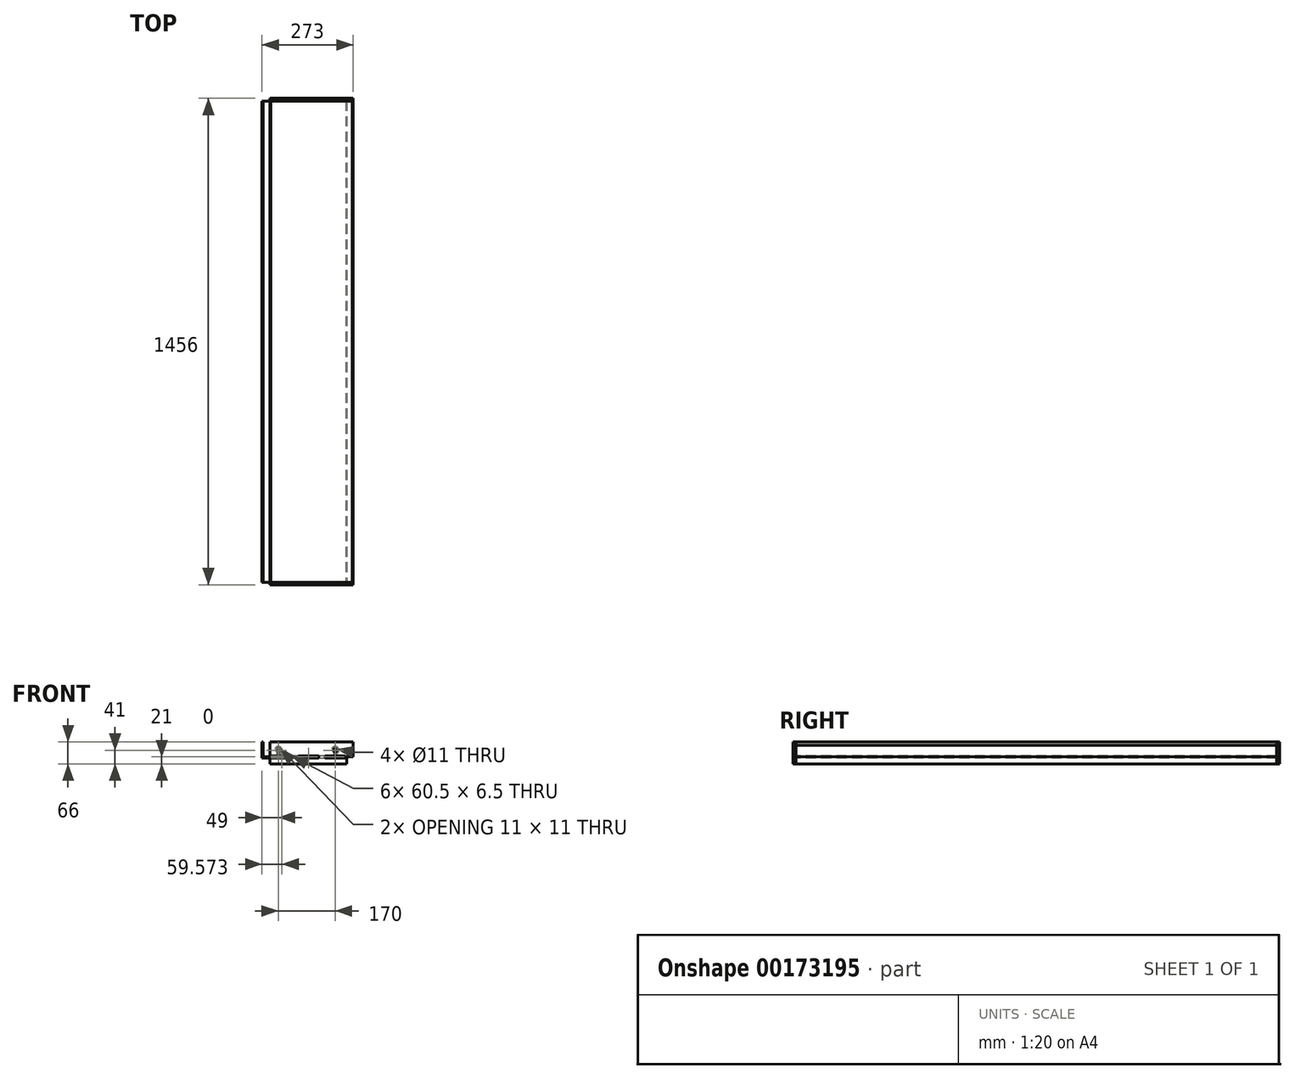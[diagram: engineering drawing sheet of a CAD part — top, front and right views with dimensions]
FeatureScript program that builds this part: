
annotation { "Feature Type Name" : "Feature", "Feature Type Description" : "" }
export const myFeature = defineFeature(function(context is Context, id is Id, definition is map)
    precondition{}
    {
        {
            var Q0;
            Q0=qCreatedBy(makeId("Front.planeOp"),FACE);
            var sketch = newSketch(context, id + "F0", { "sketchPlane" : qUnion([Q0])});
            skLineSegment(sketch, "E0", {"start": v(0, 48) * mm, "end": v(0, 0) * mm});
            skLineSegment(sketch, "E1", {"start": v(0, 0) * mm, "end": v(251, 0) * mm});
            skLineSegment(sketch, "E2", {"start": v(251, 0) * mm, "end": v(251, -18) * mm});
            skLineSegment(sketch, "E3", {"start": v(251, -18) * mm, "end": v(254, -18) * mm});
            skLineSegment(sketch, "E4", {"start": v(254, -18) * mm, "end": v(254, 3) * mm});
            skLineSegment(sketch, "E5", {"start": v(273, 3) * mm, "end": v(273, 0) * mm});
            skLineSegment(sketch, "E6", {"start": v(254, 3) * mm, "end": v(3, 3) * mm});
            skLineSegment(sketch, "E7", {"start": v(27, 48) * mm, "end": v(24, 48) * mm});
            skLineSegment(sketch, "E8", {"start": v(3, 3) * mm, "end": v(3, 48) * mm});
            skLineSegment(sketch, "E9", {"start": v(3, 48) * mm, "end": v(0, 48) * mm});
            skPoint(sketch, "E10.start.orphan", {"position": v(254, 0) * mm});
            skLineSegment(sketch, "E11", {"start": v(24, 48) * mm, "end": v(24, 3) * mm});
            skLineSegment(sketch, "E12", {"start": v(24, 3) * mm, "end": v(273, 3) * mm});
            skLineSegment(sketch, "E13", {"start": v(273, 3) * mm, "end": v(273, 6) * mm});
            skLineSegment(sketch, "E14", {"start": v(270, 6) * mm, "end": v(27, 6) * mm});
            skLineSegment(sketch, "E15", {"start": v(27, 6) * mm, "end": v(27, 48) * mm});
            skLineSegment(sketch, "E16", {"start": v(273, 6) * mm, "end": v(273, 38) * mm});
            skLineSegment(sketch, "E17", {"start": v(273, 38) * mm, "end": v(270, 38) * mm});
            skLineSegment(sketch, "E18", {"start": v(270, 38) * mm, "end": v(270, 6) * mm});
            skSolve(sketch);
        }
        {
            var Q0;
            Q0=makeQuery(id+"F0.imprint","IMPRINT",FACE,{"disambiguationData":[TD([[makeQuery(id+"F0.imprint","IMPRINT",EDGE,{"derivedFrom":sQuery(id+"F0.wireOp",EDGE,"E0")}),1.0]])]});
            extrude(context, id + "F1", {"entities" : qUnion([Q0]), "oppositeDirection" : true, "depth" : 1440 * mm});
        }
        {
            var Q0;
            Q0=makeQuery(id+"F0.imprint","IMPRINT",FACE,{"disambiguationData":[TD([[makeQuery(id+"F0.imprint","IMPRINT",EDGE,{"derivedFrom":sQuery(id+"F0.wireOp",EDGE,"E7")}),1.0]])]});
            extrude(context, id + "F2", {"entities" : qUnion([Q0]), "oppositeDirection" : true, "depth" : 1440 * mm});
        }
        {
            var Q0;
            Q0=makeQuery(id+"F2.opExtrude","SWEPT_FACE",FACE,{"disambiguationData":[OSD([sQuery(id+"F0.wireOp",EDGE,"E12")])]});
            var sketch = newSketch(context, id + "F3", { "sketchPlane" : qUnion([Q0])});
            skLineSegment(sketch, "E19.bottom", {"start": v(29.57, 7) * mm, "end": v(89.57, 7) * mm});
            skLineSegment(sketch, "E19.top", {"start": v(29.57, 0) * mm, "end": v(89.57, 0) * mm});
            skLineSegment(sketch, "E19.left", {"start": v(29.57, 7) * mm, "end": v(29.57, 0) * mm});
            skLineSegment(sketch, "E19.right", {"start": v(89.57, 7) * mm, "end": v(89.57, 0) * mm});
            skLineSegment(sketch, "E20.1.0.0", {"start": v(169.57, 7) * mm, "end": v(169.57, 0) * mm});
            skLineSegment(sketch, "E20.1.0.1", {"start": v(109.57, 7) * mm, "end": v(109.57, 0) * mm});
            skLineSegment(sketch, "E20.1.0.2", {"start": v(109.57, 0) * mm, "end": v(169.57, 0) * mm});
            skLineSegment(sketch, "E20.1.0.3", {"start": v(109.57, 7) * mm, "end": v(169.57, 7) * mm});
            skLineSegment(sketch, "E20.2.0.0", {"start": v(249, 7) * mm, "end": v(249, 0) * mm});
            skLineSegment(sketch, "E20.2.0.1", {"start": v(189, 7) * mm, "end": v(189, 0) * mm});
            skLineSegment(sketch, "E20.2.0.2", {"start": v(189, 0) * mm, "end": v(249, 0) * mm});
            skLineSegment(sketch, "E20.2.0.3", {"start": v(189, 7) * mm, "end": v(249, 7) * mm});
            skLineSegment(sketch, "E21", {"start": v(24, -720) * mm, "end": v(-373.93, -720) * mm, "construction": true});
            skLineSegment(sketch, "E22.MirrorCS", {"start": v(189, -1447) * mm, "end": v(189, -1440) * mm});
            skLineSegment(sketch, "E23.MirrorCS", {"start": v(29.57, -1447) * mm, "end": v(29.57, -1440) * mm});
            skLineSegment(sketch, "E24.MirrorCS", {"start": v(169.57, -1447) * mm, "end": v(169.57, -1440) * mm});
            skLineSegment(sketch, "E25.MirrorCS", {"start": v(109.57, -1447) * mm, "end": v(109.57, -1440) * mm});
            skLineSegment(sketch, "E26.MirrorCS", {"start": v(249, -1447) * mm, "end": v(249, -1440) * mm});
            skLineSegment(sketch, "E27.MirrorCS", {"start": v(89.57, -1447) * mm, "end": v(89.57, -1440) * mm});
            skLineSegment(sketch, "E28.MirrorCS", {"start": v(189, -1440) * mm, "end": v(249, -1440) * mm});
            skLineSegment(sketch, "E29.MirrorCS", {"start": v(109.57, -1440) * mm, "end": v(169.57, -1440) * mm});
            skLineSegment(sketch, "E30.MirrorCS", {"start": v(29.57, -1447) * mm, "end": v(89.57, -1447) * mm});
            skLineSegment(sketch, "E31.MirrorCS", {"start": v(189, -1447) * mm, "end": v(249, -1447) * mm});
            skLineSegment(sketch, "E32.MirrorCS", {"start": v(109.57, -1447) * mm, "end": v(169.57, -1447) * mm});
            skLineSegment(sketch, "E33.MirrorCS", {"start": v(29.57, -1440) * mm, "end": v(89.57, -1440) * mm});
            skSolve(sketch);
        }
        {
            var Q0;
            Q0 = qSketchRegion(id + "F3", true);
            extrude(context, id + "F4", {"entities" : qUnion([Q0]), "operationType" : NewBodyOperationType.ADD, "oppositeDirection" : true, "depth" : 3 * mm});
        }
        {
            var Q0;
            Q0=sQuery(id+"F3.wireOp",EDGE,"E21");
            cPlane(context, id + "F5", {"entities" : qUnion([Q0]), "cplaneType" : CPlaneType.LINE_ANGLE, "offset" : 25 * mm, "angle" : 0 * degree, "width" : 150 * mm, "height" : 150 * mm});
        }
        {
            var Q0;
            Q0=makeQuery(id+"F1.opExtrude","SWEPT_FACE",FACE,{"disambiguationData":[OSD([sQuery(id+"F0.wireOp",EDGE,"E1")])]});
            var sketch = newSketch(context, id + "F6", { "sketchPlane" : qUnion([Q0])});
            skLineSegment(sketch, "E34.bottom", {"start": v(249, 0) * mm, "end": v(189, 0) * mm});
            skLineSegment(sketch, "E34.top", {"start": v(249, 7) * mm, "end": v(189, 7) * mm});
            skLineSegment(sketch, "E34.left", {"start": v(249, 0) * mm, "end": v(249, 7) * mm});
            skLineSegment(sketch, "E34.right", {"start": v(189, 0) * mm, "end": v(189, 7) * mm});
            skLineSegment(sketch, "E35.bottom", {"start": v(169.57, 0) * mm, "end": v(109.57, 0) * mm});
            skLineSegment(sketch, "E35.top", {"start": v(169.57, 7) * mm, "end": v(109.57, 7) * mm});
            skLineSegment(sketch, "E35.left", {"start": v(169.57, 0) * mm, "end": v(169.57, 7) * mm});
            skLineSegment(sketch, "E35.right", {"start": v(109.57, 0) * mm, "end": v(109.57, 7) * mm});
            skLineSegment(sketch, "E36.bottom", {"start": v(89.57, 0) * mm, "end": v(29.57, 0) * mm});
            skLineSegment(sketch, "E36.top", {"start": v(89.57, 7) * mm, "end": v(29.57, 7) * mm});
            skLineSegment(sketch, "E36.left", {"start": v(89.57, 0) * mm, "end": v(89.57, 7) * mm});
            skLineSegment(sketch, "E36.right", {"start": v(29.57, 0) * mm, "end": v(29.57, 7) * mm});
            skLineSegment(sketch, "E37.MirrorCS", {"start": v(249, -1440) * mm, "end": v(249, -1447) * mm});
            skLineSegment(sketch, "E38.MirrorCS", {"start": v(29.57, -1440) * mm, "end": v(29.57, -1447) * mm});
            skLineSegment(sketch, "E39.MirrorCS", {"start": v(89.57, -1440) * mm, "end": v(89.57, -1447) * mm});
            skLineSegment(sketch, "E40.MirrorCS", {"start": v(169.57, -1440) * mm, "end": v(169.57, -1447) * mm});
            skLineSegment(sketch, "E41.MirrorCS", {"start": v(109.57, -1440) * mm, "end": v(109.57, -1447) * mm});
            skLineSegment(sketch, "E42.MirrorCS", {"start": v(189, -1440) * mm, "end": v(189, -1447) * mm});
            skLineSegment(sketch, "E43.MirrorCS", {"start": v(249, -1440) * mm, "end": v(189, -1440) * mm});
            skLineSegment(sketch, "E44.MirrorCS", {"start": v(249, -1447) * mm, "end": v(189, -1447) * mm});
            skLineSegment(sketch, "E45.MirrorCS", {"start": v(89.57, -1447) * mm, "end": v(29.57, -1447) * mm});
            skLineSegment(sketch, "E46.MirrorCS", {"start": v(169.57, -1440) * mm, "end": v(109.57, -1440) * mm});
            skLineSegment(sketch, "E47.MirrorCS", {"start": v(169.57, -1447) * mm, "end": v(109.57, -1447) * mm});
            skLineSegment(sketch, "E48.MirrorCS", {"start": v(89.57, -1440) * mm, "end": v(29.57, -1440) * mm});
            skSolve(sketch);
        }
        {
            var Q0;
            Q0 = qSketchRegion(id + "F6", true);
            extrude(context, id + "F7", {"entities" : qUnion([Q0]), "operationType" : NewBodyOperationType.ADD, "oppositeDirection" : true, "depth" : 3 * mm});
        }
        {
            var Q0;
            {var subQ8=sQuery(id+"F0.wireOp",EDGE,"E12");var subQ9=sQuery(id+"F0.wireOp",EDGE,"E6");var subQ10=sQuery(id+"F0.wireOp",EDGE,"E1");var subQ11=sQuery(id+"F0.wireOp",EDGE,"E2");var subQ16=sQuery(id+"F0.wireOp",EDGE,"E3");var subQ21=sQuery(id+"F0.wireOp",EDGE,"E4");Q0=makeQuery(id+"F7.boolean.opBoolean","SPLIT",FACE,{"disambiguationData":[TD([makeQuery(id+"F1.opExtrude","SWEPT_FACE",FACE,{"disambiguationData":[OSD([subQ11])]})])],"derivedFrom":makeQuery(id+"F1.opExtrude","CAP_FACE",FACE,{"disambiguationData":[OSD([sQuery(id+"F0.wireOp",EDGE,"E0"),subQ10,subQ11,subQ16,subQ21,subQ9,sQuery(id+"F0.wireOp",EDGE,"E8"),sQuery(id+"F0.wireOp",EDGE,"E9"),subQ8])],"isStart":true})});}
            var sketch = newSketch(context, id + "F8", { "sketchPlane" : qUnion([Q0])});
            skLineSegment(sketch, "E49", {"start": v(273, 3) * mm, "end": v(254, 3) * mm});
            skLineSegment(sketch, "E50.bottom", {"start": v(29.32, 6.25) * mm, "end": v(89.82, 6.25) * mm});
            skLineSegment(sketch, "E50.top", {"start": v(29.32, -0.25) * mm, "end": v(89.82, -0.25) * mm});
            skLineSegment(sketch, "E50.left", {"start": v(29.32, 6.25) * mm, "end": v(29.32, -0.25) * mm});
            skLineSegment(sketch, "E50.right", {"start": v(89.82, 6.25) * mm, "end": v(89.82, -0.25) * mm});
            skLineSegment(sketch, "E51.bottom", {"start": v(109.32, 6.25) * mm, "end": v(169.82, 6.25) * mm});
            skLineSegment(sketch, "E51.top", {"start": v(109.32, -0.25) * mm, "end": v(169.82, -0.25) * mm});
            skLineSegment(sketch, "E51.left", {"start": v(109.32, 6.25) * mm, "end": v(109.32, -0.25) * mm});
            skLineSegment(sketch, "E51.right", {"start": v(169.82, 6.25) * mm, "end": v(169.82, -0.25) * mm});
            skLineSegment(sketch, "E52.bottom", {"start": v(188.75, 6.25) * mm, "end": v(249.25, 6.25) * mm});
            skLineSegment(sketch, "E52.top", {"start": v(188.75, -0.25) * mm, "end": v(249.25, -0.25) * mm});
            skLineSegment(sketch, "E52.left", {"start": v(188.75, 6.25) * mm, "end": v(188.75, -0.25) * mm});
            skLineSegment(sketch, "E52.right", {"start": v(249.25, 6.25) * mm, "end": v(249.25, -0.25) * mm});
            skLineSegment(sketch, "E53.MirrorCS", {"start": v(249.25, -0.25) * mm, "end": v(249.25, 6.25) * mm});
            skLineSegment(sketch, "E54.MirrorCS", {"start": v(169.82, -0.25) * mm, "end": v(169.82, 6.25) * mm});
            skLineSegment(sketch, "E55.MirrorCS", {"start": v(109.32, -0.25) * mm, "end": v(109.32, 6.25) * mm});
            skLineSegment(sketch, "E56.MirrorCS", {"start": v(188.75, -0.25) * mm, "end": v(188.75, 6.25) * mm});
            skLineSegment(sketch, "E57.MirrorCS", {"start": v(29.32, -0.25) * mm, "end": v(29.32, 6.25) * mm});
            skLineSegment(sketch, "E58.MirrorCS", {"start": v(89.82, -0.25) * mm, "end": v(89.82, 6.25) * mm});
            skLineSegment(sketch, "E59.MirrorCS", {"start": v(273, 48) * mm, "end": v(273, 3) * mm});
            skLineSegment(sketch, "E60.MirrorCS", {"start": v(24, 48) * mm, "end": v(273, 48) * mm});
            skLineSegment(sketch, "E61", {"start": v(254, -18) * mm, "end": v(254, 3) * mm});
            skLineSegment(sketch, "E62", {"start": v(254, -18) * mm, "end": v(24, -18) * mm});
            skLineSegment(sketch, "E63", {"start": v(24, -18) * mm, "end": v(24, 48) * mm});
            skSolve(sketch);
        }
        {
            var Q0;
            Q0 = qSketchRegion(id + "F8", true);
            extrude(context, id + "F9", {"entities" : qUnion([Q0]), "depth" : 8 * mm});
        }
        {
            var Q0;
            Q0=makeQuery(id+"F9.opExtrude","SWEPT_BODY",BODY,{"disambiguationData":[OSD([sQuery(id+"F8.wireOp",EDGE,"E51.right"),sQuery(id+"F8.wireOp",EDGE,"E56.MirrorCS"),sQuery(id+"F8.wireOp",EDGE,"E51.left"),sQuery(id+"F8.wireOp",EDGE,"E50.right"),sQuery(id+"F8.wireOp",EDGE,"E51.top"),sQuery(id+"F8.wireOp",EDGE,"E51.bottom"),sQuery(id+"F8.wireOp",EDGE,"E50.bottom"),sQuery(id+"F8.wireOp",EDGE,"E50.left"),sQuery(id+"F8.wireOp",EDGE,"E53.MirrorCS"),sQuery(id+"F8.wireOp",EDGE,"E50.top"),sQuery(id+"F8.wireOp",EDGE,"8894a8ee-e391-4d04-b745-43287777c55924.MirrorCS"),sQuery(id+"F8.wireOp",EDGE,"E52.bottom"),sQuery(id+"F8.wireOp",EDGE,"E59.MirrorCS"),sQuery(id+"F8.wireOp",EDGE,"E52.top"),sQuery(id+"F8.wireOp",EDGE,"8894a8ee-e391-4d04-b745-43287777c55930.MirrorCS"),sQuery(id+"F8.wireOp",EDGE,"8894a8ee-e391-4d04-b745-43287777c55931.MirrorCS"),sQuery(id+"F8.wireOp",EDGE,"8894a8ee-e391-4d04-b745-43287777c55934.MirrorCS"),sQuery(id+"F8.wireOp",EDGE,"E60.MirrorCS")])]});
            var Q1;
            Q1=qCreatedBy(id+"F5.planeOp",FACE);
            mirror(context, id + "F10", {"entities" : qUnion([Q0]), "mirrorPlane" : qUnion([Q1])});
        }
        {
            var Q0;
            Q0=makeQuery(id+"F9.opExtrude","CAP_FACE",FACE,{"disambiguationData":[OSD([sQuery(id+"F8.wireOp",EDGE,"E51.right"),sQuery(id+"F8.wireOp",EDGE,"E56.MirrorCS"),sQuery(id+"F8.wireOp",EDGE,"E51.left"),sQuery(id+"F8.wireOp",EDGE,"E50.right"),sQuery(id+"F8.wireOp",EDGE,"E51.top"),sQuery(id+"F8.wireOp",EDGE,"E51.bottom"),sQuery(id+"F8.wireOp",EDGE,"E50.bottom"),sQuery(id+"F8.wireOp",EDGE,"E50.left"),sQuery(id+"F8.wireOp",EDGE,"E53.MirrorCS"),sQuery(id+"F8.wireOp",EDGE,"E50.top"),sQuery(id+"F8.wireOp",EDGE,"8894a8ee-e391-4d04-b745-43287777c55924.MirrorCS"),sQuery(id+"F8.wireOp",EDGE,"E52.bottom"),sQuery(id+"F8.wireOp",EDGE,"E59.MirrorCS"),sQuery(id+"F8.wireOp",EDGE,"E52.top"),sQuery(id+"F8.wireOp",EDGE,"8894a8ee-e391-4d04-b745-43287777c55930.MirrorCS"),sQuery(id+"F8.wireOp",EDGE,"8894a8ee-e391-4d04-b745-43287777c55931.MirrorCS"),sQuery(id+"F8.wireOp",EDGE,"8894a8ee-e391-4d04-b745-43287777c55934.MirrorCS"),sQuery(id+"F8.wireOp",EDGE,"E60.MirrorCS")])],"isStart":true});
            var sketch = newSketch(context, id + "F11", { "sketchPlane" : qUnion([Q0])});
            skPoint(sketch, "E64", {"position": v(-49, 23) * mm});
            skPoint(sketch, "E65", {"position": v(-219, 23) * mm});
            skSolve(sketch);
        }
        {
            var Q0;
            Q0=sQuery(id+"F11.wireOp",VERTEX,"E64");
            var Q1;
            Q1=sQuery(id+"F11.wireOp",VERTEX,"E65");
            var Q2;
            Q2=makeQuery(id+"F9.opExtrude","SWEPT_BODY",BODY,{"disambiguationData":[OSD([sQuery(id+"F8.wireOp",EDGE,"E51.right"),sQuery(id+"F8.wireOp",EDGE,"E56.MirrorCS"),sQuery(id+"F8.wireOp",EDGE,"E51.left"),sQuery(id+"F8.wireOp",EDGE,"E50.right"),sQuery(id+"F8.wireOp",EDGE,"E51.top"),sQuery(id+"F8.wireOp",EDGE,"E51.bottom"),sQuery(id+"F8.wireOp",EDGE,"E50.bottom"),sQuery(id+"F8.wireOp",EDGE,"E50.left"),sQuery(id+"F8.wireOp",EDGE,"E53.MirrorCS"),sQuery(id+"F8.wireOp",EDGE,"E50.top"),sQuery(id+"F8.wireOp",EDGE,"8894a8ee-e391-4d04-b745-43287777c55924.MirrorCS"),sQuery(id+"F8.wireOp",EDGE,"E52.bottom"),sQuery(id+"F8.wireOp",EDGE,"E59.MirrorCS"),sQuery(id+"F8.wireOp",EDGE,"E52.top"),sQuery(id+"F8.wireOp",EDGE,"8894a8ee-e391-4d04-b745-43287777c55930.MirrorCS"),sQuery(id+"F8.wireOp",EDGE,"8894a8ee-e391-4d04-b745-43287777c55931.MirrorCS"),sQuery(id+"F8.wireOp",EDGE,"8894a8ee-e391-4d04-b745-43287777c55934.MirrorCS"),sQuery(id+"F8.wireOp",EDGE,"E60.MirrorCS")])]});
            hole(context, id + "F12", {"style" : HoleStyle.C_SINK, "endStyle" : HoleEndStyle.THROUGH, "holeDiameter" : 11 * mm, "cSinkDiameter" : 22 * mm, "cSinkAngle" : 90 * degree, "locations" : qUnion([Q0, Q1]), "scope" : qUnion([Q2]), "isTappedThrough" : true});
        }
        {
            var Q0;
            Q0=makeQuery(id+"F10.opPattern","COPY",FACE,{"derivedFrom":makeQuery(id+"F9.opExtrude","CAP_FACE",FACE,{"disambiguationData":[OSD([sQuery(id+"F8.wireOp",EDGE,"E51.right"),sQuery(id+"F8.wireOp",EDGE,"E56.MirrorCS"),sQuery(id+"F8.wireOp",EDGE,"E51.left"),sQuery(id+"F8.wireOp",EDGE,"E50.right"),sQuery(id+"F8.wireOp",EDGE,"E51.top"),sQuery(id+"F8.wireOp",EDGE,"E51.bottom"),sQuery(id+"F8.wireOp",EDGE,"E50.bottom"),sQuery(id+"F8.wireOp",EDGE,"E50.left"),sQuery(id+"F8.wireOp",EDGE,"E53.MirrorCS"),sQuery(id+"F8.wireOp",EDGE,"E50.top"),sQuery(id+"F8.wireOp",EDGE,"E52.bottom"),sQuery(id+"F8.wireOp",EDGE,"E59.MirrorCS"),sQuery(id+"F8.wireOp",EDGE,"E52.top"),sQuery(id+"F8.wireOp",EDGE,"E60.MirrorCS"),sQuery(id+"F8.wireOp",EDGE,"E49"),sQuery(id+"F8.wireOp",EDGE,"E61"),sQuery(id+"F8.wireOp",EDGE,"E62"),sQuery(id+"F8.wireOp",EDGE,"E63")])],"isStart":true}),"instanceName":"1"});
            var sketch = newSketch(context, id + "F13", { "sketchPlane" : qUnion([Q0])});
            skPoint(sketch, "E66", {"position": v(49, 23) * mm});
            skPoint(sketch, "E67", {"position": v(219, 23) * mm});
            skSolve(sketch);
        }
        {
            var Q0;
            Q0=sQuery(id+"F13.wireOp",VERTEX,"E66");
            var Q1;
            Q1=sQuery(id+"F13.wireOp",VERTEX,"E67");
            var Q2;
            Q2=makeQuery(id+"F10.opPattern","COPY",BODY,{"derivedFrom":makeQuery(id+"F9.opExtrude","SWEPT_BODY",BODY,{"disambiguationData":[OSD([sQuery(id+"F8.wireOp",EDGE,"E51.right"),sQuery(id+"F8.wireOp",EDGE,"E56.MirrorCS"),sQuery(id+"F8.wireOp",EDGE,"E51.left"),sQuery(id+"F8.wireOp",EDGE,"E50.right"),sQuery(id+"F8.wireOp",EDGE,"E51.top"),sQuery(id+"F8.wireOp",EDGE,"E51.bottom"),sQuery(id+"F8.wireOp",EDGE,"E50.bottom"),sQuery(id+"F8.wireOp",EDGE,"E50.left"),sQuery(id+"F8.wireOp",EDGE,"E53.MirrorCS"),sQuery(id+"F8.wireOp",EDGE,"E50.top"),sQuery(id+"F8.wireOp",EDGE,"E52.bottom"),sQuery(id+"F8.wireOp",EDGE,"E59.MirrorCS"),sQuery(id+"F8.wireOp",EDGE,"E52.top"),sQuery(id+"F8.wireOp",EDGE,"E60.MirrorCS"),sQuery(id+"F8.wireOp",EDGE,"E49"),sQuery(id+"F8.wireOp",EDGE,"E61"),sQuery(id+"F8.wireOp",EDGE,"E62"),sQuery(id+"F8.wireOp",EDGE,"E63")])]}),"instanceName":"1"});
            hole(context, id + "F14", {"style" : HoleStyle.C_SINK, "endStyle" : HoleEndStyle.THROUGH, "holeDiameter" : 11 * mm, "cSinkDiameter" : 22 * mm, "cSinkAngle" : 90 * degree, "locations" : qUnion([Q0, Q1]), "scope" : qUnion([Q2]), "isTappedThrough" : true});
        }
    });
